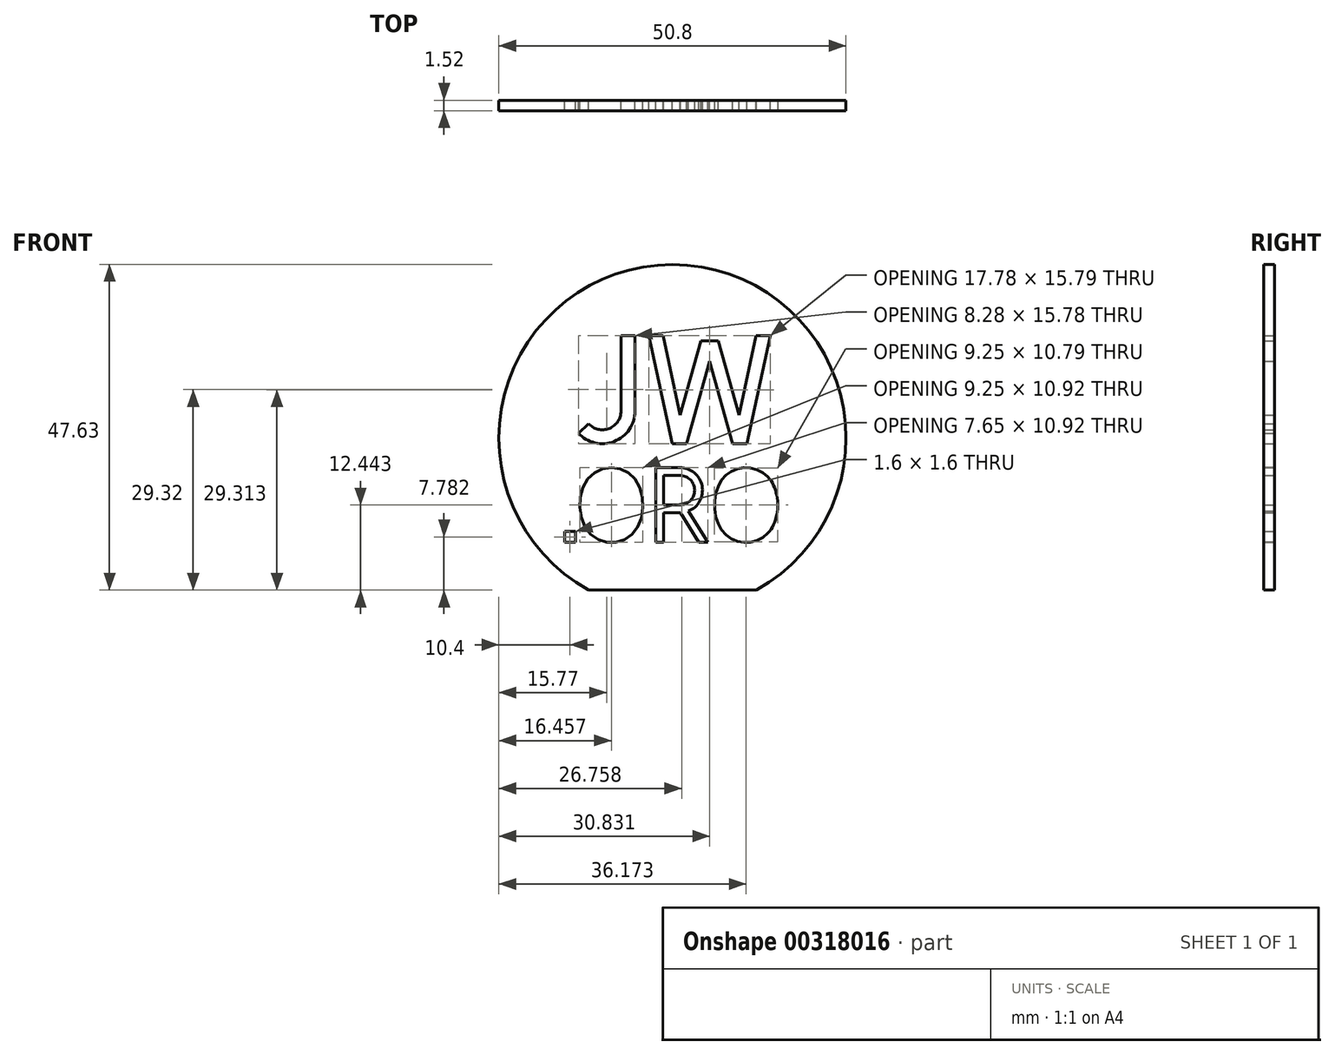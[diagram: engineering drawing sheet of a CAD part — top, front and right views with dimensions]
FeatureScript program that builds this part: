
annotation { "Feature Type Name" : "Feature", "Feature Type Description" : "" }
export const myFeature = defineFeature(function(context is Context, id is Id, definition is map)
    precondition{}
    {
        {
            var Q0;
            Q0=qCreatedBy(makeId("Front.planeOp"),FACE);
            var sketch = newSketch(context, id + "F0", { "sketchPlane" : qUnion([Q0])});
            skLineSegment(sketch, "E0.bottom", {"start": v(-46.12, 30.74) * mm, "end": v(55.48, 30.74) * mm});
            skLineSegment(sketch, "E0.top", {"start": v(-46.12, -13.7) * mm, "end": v(55.48, -13.7) * mm});
            skLineSegment(sketch, "E0.left", {"start": v(-46.12, 30.74) * mm, "end": v(-46.12, -13.7) * mm});
            skLineSegment(sketch, "E0.right", {"start": v(55.48, 30.74) * mm, "end": v(55.48, -13.7) * mm});
            skCircle(sketch, "E1", {"center": v(0, 8.52) * mm, "radius": 25.4 * mm});
            skPoint(sketch, "E1.centerSnap0", {"position": v(-46.12, 8.52) * mm});
            skLineSegment(sketch, "E2", {"start": v(0, 30.74) * mm, "end": v(0, 8.52) * mm});
            skPoint(sketch, "E2.endSnap0", {"position": v(-22.56, 8.52) * mm});
            skLineSegment(sketch, "E3", {"start": v(0, 8.52) * mm, "end": v(-22.56, 8.52) * mm});
            skLineSegment(sketch, "E4", {"start": v(-5.5, 12.48) * mm, "end": v(-5.5, 23.5) * mm});
            skLineSegment(sketch, "E5", {"start": v(-5.5, 23.5) * mm, "end": v(-7.52, 23.5) * mm});
            skLineSegment(sketch, "E6", {"start": v(-7.52, 23.5) * mm, "end": v(-7.52, 12.48) * mm});
            skArc(sketch, "E7", {"start": v(-12.27, 10.62) * mm, "mid": v(-9.27, 9.93) * mm, "end": v(-7.52, 12.48) * mm});
            skLineSegment(sketch, "E8", {"start": v(-22.56, 7.7) * mm, "end": v(-6.21, 7.7) * mm});
            skLineSegment(sketch, "E9", {"start": v(-13.77, 9.25) * mm, "end": v(-12.27, 10.62) * mm});
            skLineSegment(sketch, "E10", {"start": v(-5.5, 23.5) * mm, "end": v(-3.46, 23.5) * mm});
            skLineSegment(sketch, "E11.bottom", {"start": v(-3.46, 23.5) * mm, "end": v(14.32, 23.5) * mm});
            skLineSegment(sketch, "E11.top", {"start": v(-3.46, 7.7) * mm, "end": v(14.32, 7.7) * mm});
            skLineSegment(sketch, "E11.left", {"start": v(-3.46, 23.5) * mm, "end": v(-3.46, 7.7) * mm});
            skLineSegment(sketch, "E11.right", {"start": v(14.32, 23.5) * mm, "end": v(14.32, 7.7) * mm});
            skLineSegment(sketch, "E12", {"start": v(-3.46, 23.5) * mm, "end": v(-2.42, 23.5) * mm});
            skLineSegment(sketch, "E13", {"start": v(14.32, 23.5) * mm, "end": v(13.28, 23.5) * mm});
            skLineSegment(sketch, "E14", {"start": v(5.43, 8.37) * mm, "end": v(-3.46, 8.37) * mm});
            skPoint(sketch, "E14.startSnap0", {"position": v(5.43, 7.7) * mm});
            skLineSegment(sketch, "E15", {"start": v(0.99, 8.37) * mm, "end": v(0.99, 7.7) * mm});
            skLineSegment(sketch, "E16", {"start": v(5.43, 8.37) * mm, "end": v(14.32, 8.37) * mm});
            skLineSegment(sketch, "E17", {"start": v(9.88, 8.37) * mm, "end": v(9.88, 7.7) * mm});
            skLineSegment(sketch, "E18", {"start": v(-2.42, 23.5) * mm, "end": v(0.99, 7.7) * mm});
            skLineSegment(sketch, "E19", {"start": v(9.88, 7.7) * mm, "end": v(5.43, 23.5) * mm});
            skLineSegment(sketch, "E20", {"start": v(5.43, 23.5) * mm, "end": v(0.99, 7.7) * mm});
            skLineSegment(sketch, "E21", {"start": v(9.88, 7.7) * mm, "end": v(13.28, 23.5) * mm});
            skLineSegment(sketch, "E22.0", {"start": v(-3.46, 23.5) * mm, "end": v(-0.05, 7.7) * mm});
            skLineSegment(sketch, "E23.0", {"start": v(10.92, 7.7) * mm, "end": v(14.32, 23.5) * mm});
            skLineSegment(sketch, "E24.0", {"start": v(-1.42, 23.71) * mm, "end": v(1.12, 11.92) * mm});
            skLineSegment(sketch, "E25.0", {"start": v(6.4, 23.22) * mm, "end": v(2.04, 7.7) * mm});
            skLineSegment(sketch, "E26.0", {"start": v(8.82, 7.7) * mm, "end": v(4.45, 23.22) * mm});
            skLineSegment(sketch, "E27", {"start": v(1.12, 11.92) * mm, "end": v(1.12, 11.92) * mm});
            skLineSegment(sketch, "E28", {"start": v(9.75, 11.92) * mm, "end": v(9.75, 11.92) * mm});
            skLineSegment(sketch, "E29", {"start": v(9.75, 11.92) * mm, "end": v(6.7, 22.74) * mm});
            skLineSegment(sketch, "E30", {"start": v(9.75, 11.92) * mm, "end": v(12.29, 23.71) * mm});
            skLineSegment(sketch, "E31", {"start": v(4.16, 22.74) * mm, "end": v(6.7, 22.74) * mm});
            skLineSegment(sketch, "E32", {"start": v(4.16, 22.74) * mm, "end": v(1.12, 11.92) * mm});
            skFitSpline(sketch, "E33", {"points": [v(-8.94, 4.2) * mm, v(-12.14, 2.85) * mm, v(-13.57, -1.27) * mm, v(-12.14, -5.38) * mm, v(-8.94, -6.73) * mm, v(-5.74, -5.38) * mm, v(-4.32, -1.27) * mm, v(-5.74, 2.85) * mm, v(-8.94, 4.2) * mm]});
            skFitSpline(sketch, "E34.0", {"points": [v(-8.23, 3) * mm, v(-8.94, 3.07) * mm, v(-9.65, 3) * mm, v(-10.33, 2.8) * mm, v(-10.83, 2.5) * mm, v(-11.18, 2.2) * mm, v(-11.5, 1.87) * mm, v(-11.85, 1.34) * mm, v(-12.17, 0.56) * mm, v(-12.38, -0.33) * mm, v(-12.45, -1.27) * mm, v(-12.38, -2.2) * mm, v(-12.17, -3.1) * mm, v(-11.85, -3.88) * mm, v(-11.5, -4.4) * mm, v(-11.18, -4.74) * mm, v(-10.83, -5.04) * mm, v(-10.33, -5.32) * mm, v(-9.65, -5.54) * mm, v(-8.94, -5.6) * mm, v(-8.23, -5.54) * mm, v(-7.56, -5.32) * mm, v(-7.06, -5.04) * mm, v(-6.7, -4.74) * mm, v(-6.4, -4.4) * mm, v(-6.04, -3.88) * mm, v(-5.71, -3.1) * mm, v(-5.5, -2.2) * mm, v(-5.44, -1.27) * mm, v(-5.5, -0.33) * mm, v(-5.71, 0.56) * mm, v(-6.04, 1.34) * mm, v(-6.4, 1.87) * mm, v(-6.7, 2.2) * mm, v(-7.06, 2.5) * mm, v(-7.56, 2.8) * mm, v(-8.23, 3) * mm, v(-8.94, 3.07) * mm, v(-9.65, 3) * mm, v(-8.23, 3) * mm]});
            skLineSegment(sketch, "E35.bottom", {"start": v(-15.8, -6.73) * mm, "end": v(-14.2, -6.73) * mm});
            skLineSegment(sketch, "E35.top", {"start": v(-15.8, -5.13) * mm, "end": v(-14.2, -5.13) * mm});
            skLineSegment(sketch, "E35.left", {"start": v(-15.8, -6.73) * mm, "end": v(-15.8, -5.13) * mm});
            skLineSegment(sketch, "E35.right", {"start": v(-14.2, -6.73) * mm, "end": v(-14.2, -5.13) * mm});
            skFitSpline(sketch, "E36", {"points": [v(10.77, 4.2) * mm, v(7.57, 2.85) * mm, v(6.15, -1.27) * mm, v(7.57, -5.38) * mm, v(10.77, -6.73) * mm, v(13.97, -5.38) * mm, v(15.4, -1.27) * mm, v(13.97, 2.85) * mm, v(10.77, 4.2) * mm]});
            skFitSpline(sketch, "E37.0", {"points": [v(11.48, 3) * mm, v(10.77, 3.07) * mm, v(10.06, 3) * mm, v(9.39, 2.8) * mm, v(8.9, 2.5) * mm, v(8.54, 2.2) * mm, v(8.22, 1.87) * mm, v(7.87, 1.34) * mm, v(7.54, 0.56) * mm, v(7.34, -0.33) * mm, v(7.27, -1.27) * mm, v(7.34, -2.2) * mm, v(7.54, -3.1) * mm, v(7.87, -3.88) * mm, v(8.22, -4.4) * mm, v(8.54, -4.74) * mm, v(8.9, -5.04) * mm, v(9.39, -5.32) * mm, v(10.06, -5.54) * mm, v(10.77, -5.6) * mm, v(11.48, -5.54) * mm, v(12.16, -5.32) * mm, v(12.66, -5.04) * mm, v(13, -4.74) * mm, v(13.32, -4.4) * mm, v(13.68, -3.88) * mm, v(14, -3.1) * mm, v(14.2, -2.2) * mm, v(14.28, -1.27) * mm, v(14.2, -0.33) * mm, v(14, 0.56) * mm, v(13.68, 1.34) * mm, v(13.32, 1.87) * mm, v(13, 2.2) * mm, v(12.66, 2.5) * mm, v(12.16, 2.8) * mm, v(11.48, 3) * mm, v(10.77, 3.07) * mm, v(10.06, 3) * mm]});
            skLineSegment(sketch, "E38", {"start": v(13.26, 1.93) * mm, "end": v(13.97, 2.85) * mm});
            skPoint(sketch, "E39.orphan", {"position": v(10.77, -1.27) * mm});
            skLineSegment(sketch, "E40", {"start": v(13.97, -5.38) * mm, "end": v(13.97, -1.27) * mm});
            skLineSegment(sketch, "E41", {"start": v(13.97, -1.27) * mm, "end": v(10.77, -1.27) * mm});
            skLineSegment(sketch, "E42", {"start": v(10.77, -1.27) * mm, "end": v(10.77, -2.41) * mm});
            skLineSegment(sketch, "E43", {"start": v(10.77, -2.41) * mm, "end": v(12.83, -2.41) * mm});
            skLineSegment(sketch, "E44", {"start": v(12.83, -2.41) * mm, "end": v(12.83, -4.89) * mm});
            skLineSegment(sketch, "E45", {"start": v(-2.47, -6.73) * mm, "end": v(-2.47, 4.2) * mm});
            skLineSegment(sketch, "E46", {"start": v(-2.47, 4.2) * mm, "end": v(1.1, 4.2) * mm});
            skLineSegment(sketch, "E47", {"start": v(-2.47, -1.27) * mm, "end": v(1.14, -1.27) * mm});
            skLineSegment(sketch, "E48.0", {"start": v(-1.32, -2.4) * mm, "end": v(1.15, -2.4) * mm});
            skLineSegment(sketch, "E49", {"start": v(-2.47, -6.73) * mm, "end": v(-1.32, -6.73) * mm});
            skLineSegment(sketch, "E50.0", {"start": v(-1.32, 3.05) * mm, "end": v(1.1, 3.05) * mm});
            skArc(sketch, "E51", {"start": v(1.14, -1.27) * mm, "mid": v(3.25, 0.92) * mm, "end": v(1.1, 3.05) * mm});
            skLineSegment(sketch, "E52", {"start": v(-1.32, -6.73) * mm, "end": v(-1.32, -2.4) * mm});
            skLineSegment(sketch, "E53", {"start": v(-1.32, -1.27) * mm, "end": v(-1.32, 3.05) * mm});
            skArc(sketch, "E54", {"start": v(-13.77, 9.25) * mm, "mid": v(-8.53, 8.03) * mm, "end": v(-5.5, 12.48) * mm});
            skLineSegment(sketch, "E55", {"start": v(1.15, -2.4) * mm, "end": v(3.84, -6.73) * mm});
            skLineSegment(sketch, "E56", {"start": v(3.84, -6.73) * mm, "end": v(5.18, -6.73) * mm});
            skLineSegment(sketch, "E57", {"start": v(5.18, -6.73) * mm, "end": v(2.34, -2.16) * mm});
            skArc(sketch, "E58.trimOffspring", {"start": v(2.34, -2.16) * mm, "mid": v(4.33, 1.53) * mm, "end": v(1.1, 4.2) * mm});
            skPoint(sketch, "E59", {"position": v(-10.26, 7.7) * mm});
            skPoint(sketch, "E60", {"position": v(25.4, -16.88) * mm});
            skPoint(sketch, "E61", {"position": v(-15, -5.93) * mm});
            skPoint(sketch, "E61.positionSnap0", {"position": v(-15, -6.73) * mm});
            skPoint(sketch, "E61.positionSnap1", {"position": v(-14.2, -5.93) * mm});
            skSolve(sketch);
        }
        {
            var Q0;
            {var subQ0=sQuery(id+"F0.wireOp",EDGE,"E0.bottom");var subQ1=makeQuery(id+"F0.imprint","IMPRINT",VERTEX,{"derivedFrom":subQ0});Q0=makeQuery(id+"F0.imprint","IMPRINT",FACE,{"disambiguationData":[TD([[makeQuery(id+"F0.imprint","IMPRINT",EDGE,{"disambiguationData":[TD([[subQ1,1.0]])],"derivedFrom":subQ0}),1.0]])]});}
            var Q1;
            {var subQ0=sQuery(id+"F0.wireOp",EDGE,"E1");var subQ1=sQuery(id+"F0.wireOp",EDGE,"E0.top");var subQ2=makeQuery(id+"F0.imprint","INTERSECT",VERTEX,{"disambiguationData":[OD(0.0)],"derivedFrom":[subQ1,subQ0]});Q1=makeQuery(id+"F0.imprint","IMPRINT",FACE,{"disambiguationData":[TD([[makeQuery(id+"F0.imprint","IMPRINT",EDGE,{"disambiguationData":[TD([[subQ2,-1.0]])],"derivedFrom":subQ1}),-1.0]])]});}
            var Q2;
            Q2=makeQuery(id+"F0.imprint","IMPRINT",FACE,{"disambiguationData":[TD([[makeQuery(id+"F0.imprint","IMPRINT",EDGE,{"derivedFrom":sQuery(id+"F0.wireOp",EDGE,"E5")}),-1.0]])]});
            var Q3;
            {var subQ2=sQuery(id+"F0.wireOp",EDGE,"E4");Q3=makeQuery(id+"F0.imprint","IMPRINT",FACE,{"disambiguationData":[TD([[makeQuery(id+"F0.imprint","IMPRINT",EDGE,{"derivedFrom":subQ2}),-1.0]])]});}
            var Q4;
            {var subQ0=sQuery(id+"F0.wireOp",EDGE,"E22.0");var subQ1=sQuery(id+"F0.wireOp",EDGE,"E3");var subQ2=makeQuery(id+"F0.imprint","INTERSECT",VERTEX,{"derivedFrom":[subQ1,subQ0]});Q4=makeQuery(id+"F0.imprint","IMPRINT",FACE,{"disambiguationData":[TD([[makeQuery(id+"F0.imprint","IMPRINT",EDGE,{"disambiguationData":[TD([[subQ2,-1.0]])],"derivedFrom":subQ1}),-1.0]])]});}
            var Q5;
            {var subQ0=sQuery(id+"F0.wireOp",EDGE,"E32");Q5=makeQuery(id+"F0.imprint","IMPRINT",FACE,{"disambiguationData":[TD([[makeQuery(id+"F0.imprint","IMPRINT",EDGE,{"derivedFrom":subQ0}),-1.0]])]});}
            var Q6;
            {var subQ0=sQuery(id+"F0.wireOp",EDGE,"E11.bottom");var subQ1=sQuery(id+"F0.wireOp",EDGE,"E2");var subQ2=makeQuery(id+"F0.imprint","INTERSECT",VERTEX,{"derivedFrom":[subQ1,subQ0]});Q6=makeQuery(id+"F0.imprint","IMPRINT",FACE,{"disambiguationData":[TD([[makeQuery(id+"F0.imprint","IMPRINT",EDGE,{"disambiguationData":[TD([[subQ2,-1.0]])],"derivedFrom":subQ1}),-1.0]])]});}
            var Q7;
            {var subQ0=sQuery(id+"F0.wireOp",EDGE,"E11.left");var subQ1=sQuery(id+"F0.wireOp",EDGE,"E11.top");var subQ2=makeQuery(id+"F0.imprint","INTERSECT",VERTEX,{"derivedFrom":[subQ1,subQ0]});Q7=makeQuery(id+"F0.imprint","IMPRINT",FACE,{"disambiguationData":[TD([[makeQuery(id+"F0.imprint","IMPRINT",EDGE,{"disambiguationData":[TD([[subQ2,-1.0]])],"derivedFrom":subQ1}),1.0]])]});}
            var Q8;
            {var subQ0=sQuery(id+"F0.wireOp",EDGE,"E22.0");var subQ1=sQuery(id+"F0.wireOp",EDGE,"E3");var subQ2=makeQuery(id+"F0.imprint","INTERSECT",VERTEX,{"derivedFrom":[subQ1,subQ0]});Q8=makeQuery(id+"F0.imprint","IMPRINT",FACE,{"disambiguationData":[TD([[makeQuery(id+"F0.imprint","IMPRINT",EDGE,{"disambiguationData":[TD([[subQ2,-1.0]])],"derivedFrom":subQ1}),1.0]])]});}
            var Q9;
            {var subQ0=sQuery(id+"F0.wireOp",EDGE,"E16");var subQ1=sQuery(id+"F0.wireOp",EDGE,"E14");var subQ2=makeQuery(id+"F0.imprint","INTERSECT",VERTEX,{"derivedFrom":[subQ1,subQ0]});Q9=makeQuery(id+"F0.imprint","IMPRINT",FACE,{"disambiguationData":[TD([[makeQuery(id+"F0.imprint","IMPRINT",EDGE,{"disambiguationData":[TD([[subQ2,-1.0]])],"derivedFrom":subQ1}),-1.0]])]});}
            var Q10;
            {var subQ1=sQuery(id+"F0.wireOp",EDGE,"E29");Q10=makeQuery(id+"F0.imprint","IMPRINT",FACE,{"disambiguationData":[TD([[makeQuery(id+"F0.imprint","IMPRINT",EDGE,{"derivedFrom":subQ1}),-1.0]])]});}
            var Q11;
            {var subQ0=sQuery(id+"F0.wireOp",EDGE,"E13");var subQ1=sQuery(id+"F0.wireOp",EDGE,"E11.right");var subQ2=makeQuery(id+"F0.imprint","INTERSECT",VERTEX,{"derivedFrom":[subQ1,subQ0]});Q11=makeQuery(id+"F0.imprint","IMPRINT",FACE,{"disambiguationData":[TD([[makeQuery(id+"F0.imprint","IMPRINT",EDGE,{"disambiguationData":[TD([[subQ2,-1.0]])],"derivedFrom":subQ1}),-1.0]])]});}
            var Q12;
            {var subQ1=sQuery(id+"F0.wireOp",EDGE,"E19");var subQ3=sQuery(id+"F0.wireOp",EDGE,"E31");var subQ4=makeQuery(id+"F0.imprint","INTERSECT",VERTEX,{"derivedFrom":[subQ1,subQ3]});Q12=makeQuery(id+"F0.imprint","IMPRINT",FACE,{"disambiguationData":[TD([[makeQuery(id+"F0.imprint","IMPRINT",EDGE,{"disambiguationData":[TD([[subQ4,1.0]])],"derivedFrom":subQ3}),1.0]])]});}
            var Q13;
            {var subQ0=sQuery(id+"F0.wireOp",EDGE,"E11.right");var subQ1=sQuery(id+"F0.wireOp",EDGE,"E11.top");var subQ2=makeQuery(id+"F0.imprint","INTERSECT",VERTEX,{"derivedFrom":[subQ1,subQ0]});Q13=makeQuery(id+"F0.imprint","IMPRINT",FACE,{"disambiguationData":[TD([[makeQuery(id+"F0.imprint","IMPRINT",EDGE,{"disambiguationData":[TD([[subQ2,1.0]])],"derivedFrom":subQ1}),1.0]])]});}
            var Q14;
            {var subQ3=sQuery(id+"F0.wireOp",EDGE,"E25.0");var subQ5=sQuery(id+"F0.wireOp",EDGE,"E11.top");var subQ6=makeQuery(id+"F0.imprint","INTERSECT",VERTEX,{"derivedFrom":[subQ5,subQ3]});Q14=makeQuery(id+"F0.imprint","IMPRINT",FACE,{"disambiguationData":[TD([[makeQuery(id+"F0.imprint","IMPRINT",EDGE,{"disambiguationData":[TD([[subQ6,-1.0]])],"derivedFrom":subQ5}),1.0]])]});}
            var Q15;
            Q15=makeQuery(id+"F0.imprint","IMPRINT",FACE,{"disambiguationData":[TD([[makeQuery(id+"F0.imprint","IMPRINT",EDGE,{"derivedFrom":sQuery(id+"F0.wireOp",EDGE,"E50.0")}),-1.0]])]});
            var Q16;
            Q16=makeQuery(id+"F0.imprint","IMPRINT",FACE,{"disambiguationData":[TD([[makeQuery(id+"F0.imprint","IMPRINT",EDGE,{"derivedFrom":sQuery(id+"F0.wireOp",EDGE,"E34.0")}),1.0]])]});
            extrude(context, id + "F1", {"entities" : qUnion([Q0, Q1, Q2, Q3, Q4, Q5, Q6, Q7, Q8, Q9, Q10, Q11, Q12, Q13, Q14, Q15, Q16]), "depth" : 1.52 * mm});
        }
        {
            var Q0;
            Q0=makeQuery(id+"F1.opExtrude","CAP_FACE",FACE,{"disambiguationData":[OSD([sQuery(id+"F0.wireOp",EDGE,"E1"),sQuery(id+"F0.wireOp",EDGE,"E4"),sQuery(id+"F0.wireOp",EDGE,"E5"),sQuery(id+"F0.wireOp",EDGE,"E6"),sQuery(id+"F0.wireOp",EDGE,"E7"),sQuery(id+"F0.wireOp",EDGE,"E9"),sQuery(id+"F0.wireOp",EDGE,"E11.bottom"),sQuery(id+"F0.wireOp",EDGE,"E11.top"),sQuery(id+"F0.wireOp",EDGE,"E12"),sQuery(id+"F0.wireOp",EDGE,"E13"),sQuery(id+"F0.wireOp",EDGE,"E22.0"),sQuery(id+"F0.wireOp",EDGE,"E23.0"),sQuery(id+"F0.wireOp",EDGE,"E24.0"),sQuery(id+"F0.wireOp",EDGE,"E25.0"),sQuery(id+"F0.wireOp",EDGE,"E26.0"),sQuery(id+"F0.wireOp",EDGE,"E29"),sQuery(id+"F0.wireOp",EDGE,"E30"),sQuery(id+"F0.wireOp",EDGE,"E31"),sQuery(id+"F0.wireOp",EDGE,"E32"),sQuery(id+"F0.wireOp",EDGE,"E33"),sQuery(id+"F0.wireOp",EDGE,"E35.bottom"),sQuery(id+"F0.wireOp",EDGE,"E35.top"),sQuery(id+"F0.wireOp",EDGE,"E35.left"),sQuery(id+"F0.wireOp",EDGE,"E35.right"),sQuery(id+"F0.wireOp",EDGE,"E36"),sQuery(id+"F0.wireOp",EDGE,"E37.0"),sQuery(id+"F0.wireOp",EDGE,"E38"),sQuery(id+"F0.wireOp",EDGE,"E40"),sQuery(id+"F0.wireOp",EDGE,"E41"),sQuery(id+"F0.wireOp",EDGE,"E42"),sQuery(id+"F0.wireOp",EDGE,"E43"),sQuery(id+"F0.wireOp",EDGE,"E44"),sQuery(id+"F0.wireOp",EDGE,"E45"),sQuery(id+"F0.wireOp",EDGE,"E46"),sQuery(id+"F0.wireOp",EDGE,"E48.0"),sQuery(id+"F0.wireOp",EDGE,"E49"),sQuery(id+"F0.wireOp",EDGE,"E52"),sQuery(id+"F0.wireOp",EDGE,"E54"),sQuery(id+"F0.wireOp",EDGE,"E55"),sQuery(id+"F0.wireOp",EDGE,"E56"),sQuery(id+"F0.wireOp",EDGE,"E57"),sQuery(id+"F0.wireOp",EDGE,"E58.trimOffspring")])],"isStart":false});
            var sketch = newSketch(context, id + "F2", { "sketchPlane" : qUnion([Q0])});
            skLineSegment(sketch, "E62", {"start": v(-5.5, 23.5) * mm, "end": v(-6.5, 22.48) * mm});
            skPoint(sketch, "E62.endSnap0", {"position": v(-6.5, 23.5) * mm});
            skLineSegment(sketch, "E63", {"start": v(0, -16.88) * mm, "end": v(25.4, -16.88) * mm});
            skLineSegment(sketch, "E64", {"start": v(25.4, -16.88) * mm, "end": v(25.4, 8.52) * mm});
            skPoint(sketch, "E65", {"position": v(-7.52, 12.48) * mm});
            skPoint(sketch, "E66", {"position": v(-10.26, 12.48) * mm});
            skSolve(sketch);
        }
    });
